# Revit family: WashbasinUnit-130cm-With2Drawer-WithVanity-WithDoubleWashbasin-WithoutLegs-Vitra-SentoSeries-62373+62374+62375+62376+62377+62378+62379+62380+62381
name_source: partatom
category: Furniture Systems
revit_build: Autodesk Revit 2017 (Build: 20160225_1515(x64)
units: mm (PartAtom-declared; Revit-internal decimal feet)

## family parameters
Cut with Voids When Loaded = No
Host = Face
OmniClass Number = 23.40.00.00
OmniClass Title = Equipment and Furnishings
Part Type = Normal
Room Calculation Point = No
Round Connector Dimension = Use Diameter
Shared = Yes

## types (9) — shared parameters
Ambience Led Lighting = 220V
BIMobject category = Bathroom compound units
Construction Type = Face Mounted
Default Elevation = 705 mm  [stored 2.31299 ft]
Depth(mm) = 445 mm  [stored 1.45997 ft]
Design country = Turkey
Height(mm) = 705 mm  [stored 2.31299 ft]
IFC Classification = Furniture
Manufacturer = Vitra
Manufacturer name = Vitra
Masterformat 2014 Code = 13 42 13
Masterformat 2014 Description = Bathroom Unit Modules
NBS Referans Code = 35-75-08
NBS Referans Description = Bathroom Cabinets
Nominal height = 0.000
Nominal width = 0.000
OmniClass Code = 23-31 25 13
OmniClass Description = Bathroom Cabinets
Primary Material = oak
Product certification = https://vitraglobal.com
Product family = Sento
Product group = Washbasin Unit
Technical description = https://www.vitraglobal.com
UNSPSC Code = 301815
UNSPSC Description = Bathroom Cabinets
URL = https://vitraglobal.com
Uniclass 1.4 Code = L8241
Uniclass 1.4 Description = Bathroom Cabinets
Uniclass 2.0 Code = PR-35-75-08
Uniclass 2.0 Description = Bathroom Cabinets
Uniclass 2015 Code = Pr_40_20_93
Uniclass 2015 Name = Wash basins, sinks and troughs
Uniformat II Code = E20
Uniformat II Description = FURNISHINGS
Warranty Period (Year) = 2
Weight Net (kg) = 99,000
Width(mm) = 1220 mm  [stored 4.00262 ft]
Without legs = No
Youtube = https://www.youtube.com

## per-type parameters (varying)
| type | Article No. (default) | Description | Left | Model | Product SKU | Product data url | Product url | Right | Secondary Material |
| Sento Washbasin Unit, 130 cm, with vanity washbasin, with 2 drawer, with doublewashbasin, without legs, MatteWhite-62373 | 62373 | Sento Washbasin Unit, 130 cm, with vanity washbasin, with 2 drawer, with double washbasin, without legs, | No | 62373 | 62373 | https://www.bimobject.com | https://www.vitraglobal.com | No | White |
| Sento Washbasin Unit, 130 cm, with vanity washbasin, with 2 drawer, with doublewashbasin, without legs, MatteCream -62374 | 62374 | Sento Washbasin Unit, 130 cm, with vanity washbasin, with 2 drawer, with double washbasin, without legs, | No | 62374 | 62374 | https://www.vitraglobal.com |  | No | Matte Cream |
| Sento Washbasin Unit, 130 cm, with vanity washbasin, with 2 drawer, with doublewashbasin, without legs, MatteAnthracite -62375 | 62375 | Sento Washbasin Unit, 130 cm, with vanity washbasin, with 2 drawer, with double washbasin, without legs, | No | 62375 | 62375 | https://www.vitraglobal.com |  | No | Matte Antrasit |
| Sento Washbasin Unit, 130 cm, with vanity washbasin, with 2 drawer, with doublewashbasin, without legs, Right-MatteWhite-62376 | 62376 | Sento Washbasin Unit, 130 cm, with vanity washbasin, with 2 drawer, with double washbasin, Right without legs, | No | 62376 | 62376 | https://www.vitraglobal.com |  | Yes | White |
| Sento Washbasin Unit, 130 cm, with vanity washbasin, with 2 drawer, with doublewashbasin, without legs, Right-MatteCream-62377 | 62377 | Sento Washbasin Unit, 130 cm, with vanity washbasin, with 2 drawer, with double washbasin, Right without legs, | No | 62377 | 62377 | https://www.vitraglobal.com |  | Yes | Matte Cream |
| Sento Washbasin Unit, 130 cm, with vanity washbasin, with 2 drawer, with doublewashbasin, without legs, Right-MatteAnthracite-62378 | 62378 | Sento Washbasin Unit, 130 cm, with vanity washbasin, with 2 drawer, with double washbasin, Right without legs, | No | 62378 | 62378 | https://www.vitraglobal.com |  | Yes | Matte Antrasit |
| Sento Washbasin Unit, 130 cm, with vanity washbasin, with 2 drawer, with doublewashbasin, without legs, Left-MatteWhite-62379 | 62379 | Sento Washbasin Unit, 130 cm, with vanity washbasin, with 2 drawer, with double washbasin, Left without legs, | Yes | 62379 | 62379 | https://www.vitraglobal.com |  | No | White |
| Sento Washbasin Unit, 130 cm, with vanity washbasin, with 2 drawer, with doublewashbasin, without legs, Left-MatteCream-62380 | 62380 | Sento Washbasin Unit, 130 cm, with vanity washbasin, with 2 drawer, with double washbasin, Left without legs, | Yes | 62380 | 62380 | https://www.vitraglobal.com |  | No | Matte Cream |
| Sento Washbasin Unit, 130 cm, with vanity washbasin, with 2 drawer, with doublewashbasin, without legs, Left-MatteAnthracite-62381 | 62381 | Sento Washbasin Unit, 130 cm, with vanity washbasin, with 2 drawer, with double washbasin, Left without legs, | Yes | 62381 | 62381 | https://www.vitraglobal.com |  | No | Matte Antrasit |

note: [stored X ft] marks values corroborated as IEEE doubles in the binary element streams (Revit-internal decimal feet)

## geometry (parser evidence)
native form markers: Sweep x2
no freeform markers — native parametric forms only
